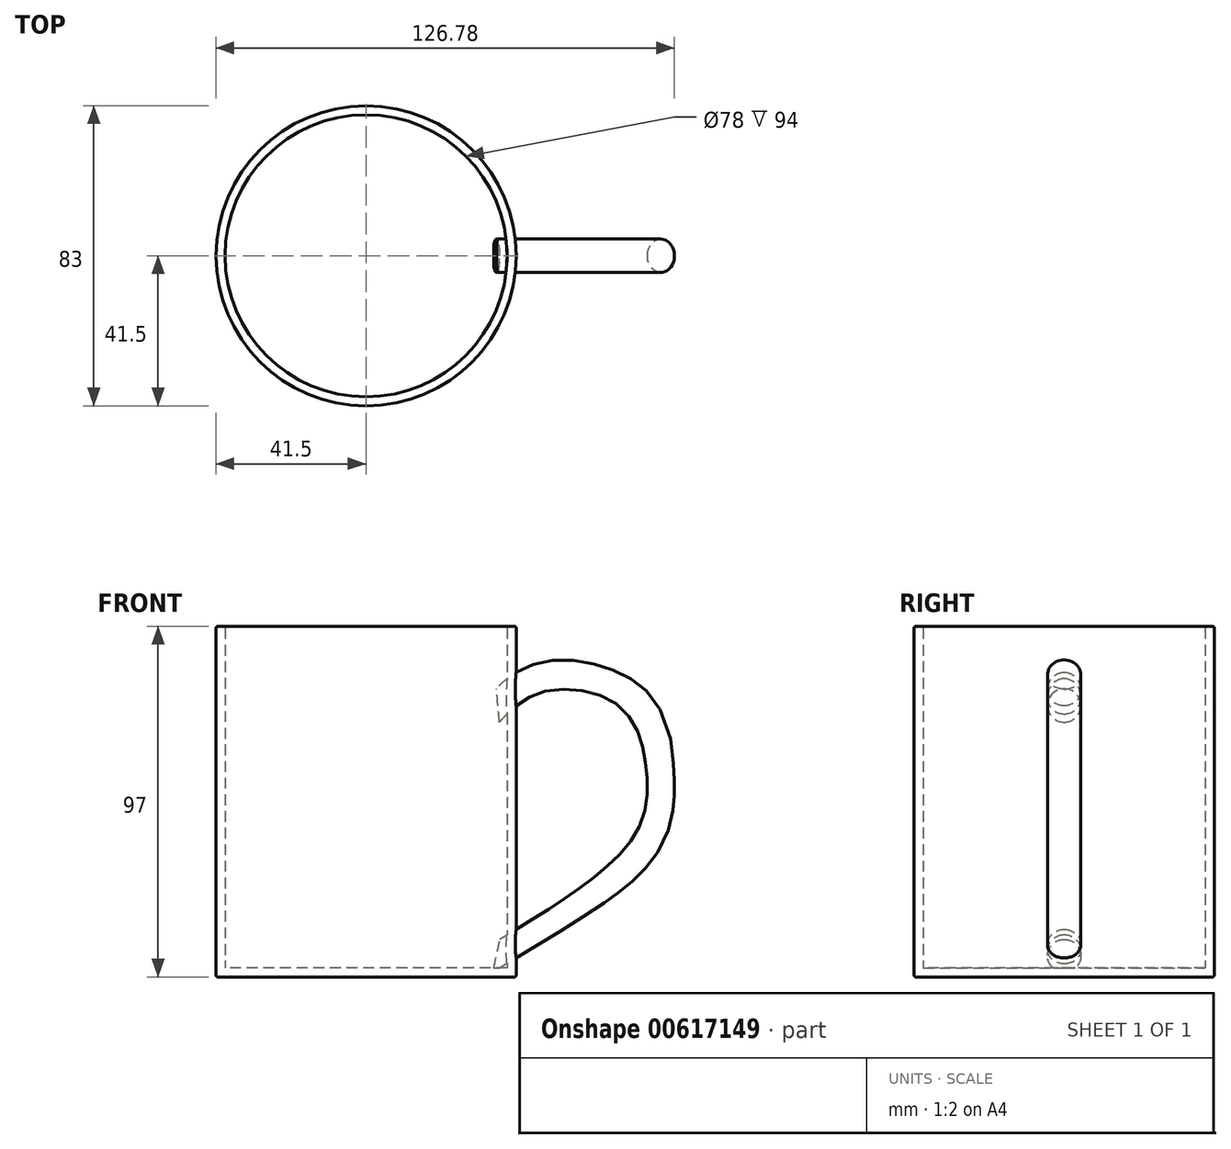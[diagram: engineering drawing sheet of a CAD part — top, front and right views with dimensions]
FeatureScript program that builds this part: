
annotation { "Feature Type Name" : "Feature", "Feature Type Description" : "" }
export const myFeature = defineFeature(function(context is Context, id is Id, definition is map)
    precondition{}
    {
        {
            var Q0;
            Q0=qCreatedBy(makeId("Top.planeOp"),FACE);
            var sketch = newSketch(context, id + "F0", { "sketchPlane" : qUnion([Q0])});
            skCircle(sketch, "E0", {"center": v(0, 0) * mm, "radius": 41.5 * mm});
            skSolve(sketch);
        }
        {
            var Q0;
            Q0=makeQuery(id+"F0.imprint","IMPRINT",FACE,{"disambiguationData":[TD([[makeQuery(id+"F0.imprint","IMPRINT",EDGE,{"derivedFrom":sQuery(id+"F0.wireOp",EDGE,"E0")}),1.0]])]});
            extrude(context, id + "F1", {"entities" : qUnion([Q0]), "depth" : 97 * mm, "offsetDistance" : 25 * mm});
        }
        {
            var Q0;
            Q0=qCreatedBy(makeId("Right.planeOp"),FACE);
            cPlane(context, id + "F2", {"entities" : qUnion([Q0]), "cplaneType" : CPlaneType.OFFSET, "offset" : 41.5 * mm, "width" : 150 * mm, "height" : 150 * mm});
        }
        {
            var Q0;
            Q0=makeQuery(id+"F1.opExtrude","CAP_FACE",FACE,{"disambiguationData":[OSD([sQuery(id+"F0.wireOp",EDGE,"E0")])],"isStart":false});
            shell(context, id + "F3", {"entities" : qUnion([Q0]), "thickness" : 2.5 * mm});
        }
        {
            var Q0;
            {var subQ0=sQuery(id+"F0.wireOp",EDGE,"E0");Q0=makeQuery(id+"F3.opShell","OFFSET_EDGE",EDGE,{"disambiguationData":[OSD([subQ0]),TDD([makeQuery(id+"F1.opExtrude","CAP_EDGE",EDGE,{"disambiguationData":[OSD([subQ0])],"isStart":false})])]});}
            fillet(context, id + "F4", {"entities" : qUnion([Q0]), "radius" : 0.5 * mm, "tangentPropagation" : true, "allowEdgeOverflow" : false});
        }
        {
            var Q0;
            Q0=makeQuery(id+"F1.opExtrude","SWEPT_FACE",FACE,{"disambiguationData":[OSD([sQuery(id+"F0.wireOp",EDGE,"E0")])]});
            fillet(context, id + "F5", {"entities" : qUnion([Q0]), "radius" : 0.5 * mm, "tangentPropagation" : true, "allowEdgeOverflow" : false});
        }
        {
            var Q0;
            Q0=qCreatedBy(id+"F2.planeOp",FACE);
            var sketch = newSketch(context, id + "F6", { "sketchPlane" : qUnion([Q0])});
            skCircle(sketch, "E1", {"center": v(0, 79.65) * mm, "radius": 4.63 * mm});
            skSolve(sketch);
        }
        {
            var Q0;
            Q0=qCreatedBy(makeId("Front.planeOp"),FACE);
            var sketch = newSketch(context, id + "F7", { "sketchPlane" : qUnion([Q0])});
            skFitSpline(sketch, "E2", {"points": [v(37.3, 65.72) * mm, v(49.07, 75.04) * mm, v(66.56, 72.85) * mm, v(73.44, 60.43) * mm, v(72.7, 44.32) * mm, v(60.56, 30.07) * mm, v(38.03, 15.06) * mm], "startDerivative": vector(66.04, 75.63) * mm, "endDerivative": vector(-116.53, -71.82) * mm});
            skSolve(sketch);
        }
        {
            var Q0;
            Q0=makeQuery(id+"F6.imprint","IMPRINT",FACE,{"disambiguationData":[TD([[makeQuery(id+"F6.imprint","IMPRINT",EDGE,{"derivedFrom":sQuery(id+"F6.wireOp",EDGE,"E1")}),1.0]])]});
            var Q1;
            Q1=sQuery(id+"F7.wireOp",EDGE,"E2");
            sweep(context, id + "F8", {"operationType" : NewBodyOperationType.ADD, "profiles" : qUnion([Q0]), "path" : qUnion([Q1])});
        }
    });
